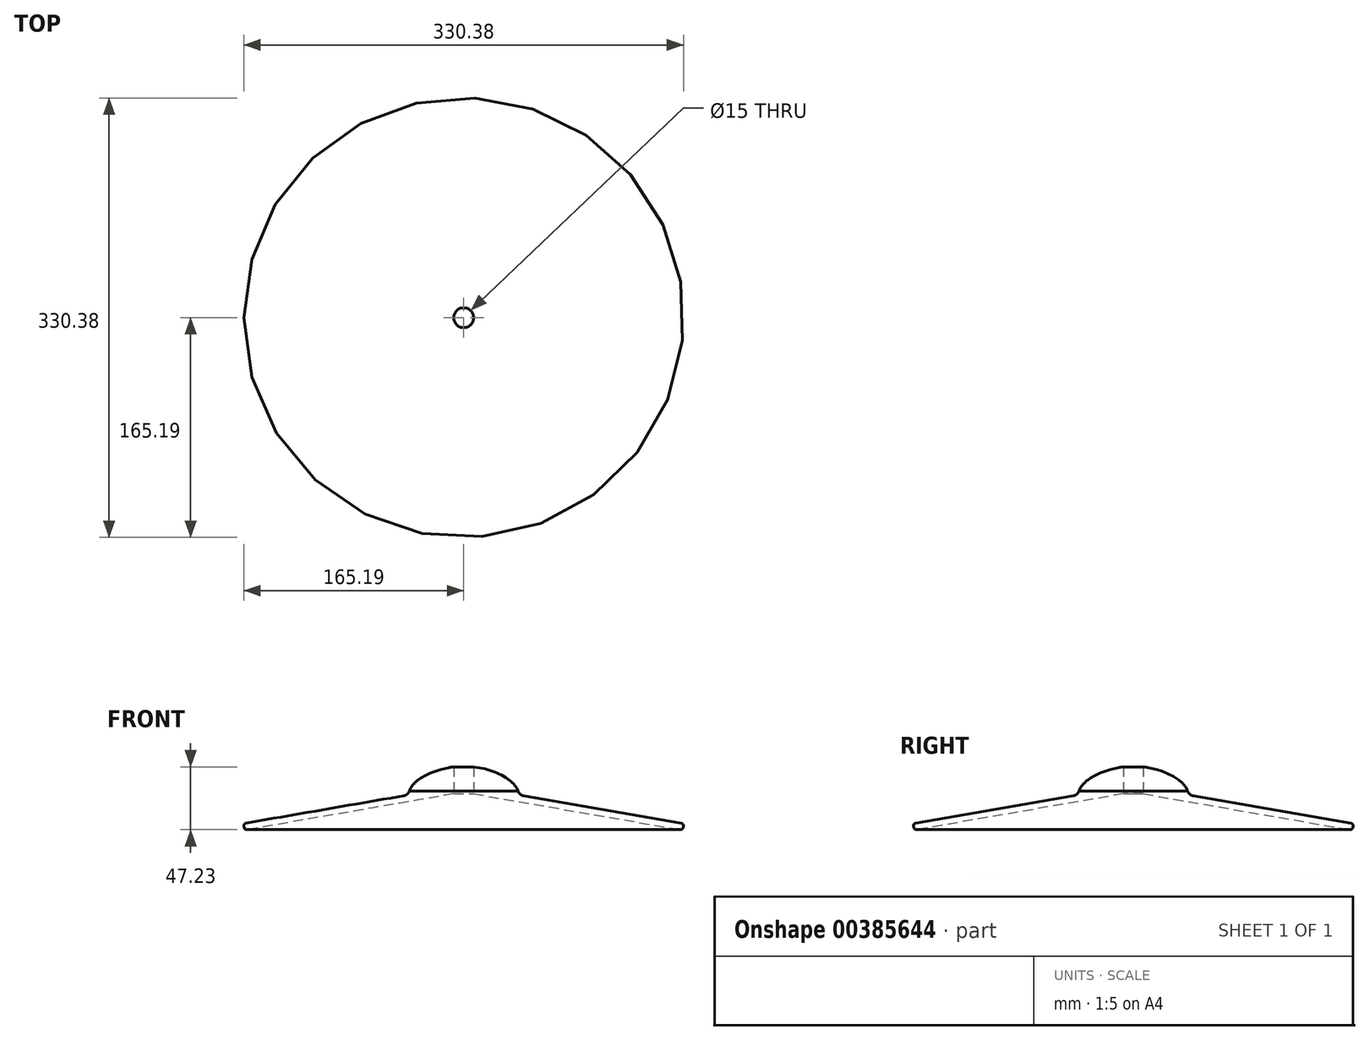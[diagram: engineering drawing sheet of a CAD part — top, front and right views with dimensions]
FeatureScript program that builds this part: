
annotation { "Feature Type Name" : "Feature", "Feature Type Description" : "" }
export const myFeature = defineFeature(function(context is Context, id is Id, definition is map)
    precondition{}
    {
        {
            var Q0;
            Q0=qCreatedBy(makeId("Front.planeOp"),FACE);
            var sketch = newSketch(context, id + "F0", { "sketchPlane" : qUnion([Q0])});
            skLineSegment(sketch, "E0", {"start": v(41.37, 0) * mm, "end": v(165.5, -21.54) * mm});
            skLineSegment(sketch, "E1", {"start": v(165.5, -21.54) * mm, "end": v(164.65, -26.46) * mm});
            skLineSegment(sketch, "E2", {"start": v(164.65, -26.46) * mm, "end": v(0, 2.1) * mm});
            skLineSegment(sketch, "E3", {"start": v(0, 21.54) * mm, "end": v(0, -26.46) * mm, "construction": true});
            skLineSegment(sketch, "E4.bottom", {"start": v(-165.5, 21.54) * mm, "end": v(165.5, 21.54) * mm, "construction": true});
            skLineSegment(sketch, "E4.top", {"start": v(-165.5, -26.46) * mm, "end": v(165.5, -26.46) * mm, "construction": true});
            skLineSegment(sketch, "E4.left", {"start": v(-165.5, 21.54) * mm, "end": v(-165.5, -26.46) * mm, "construction": true});
            skLineSegment(sketch, "E4.right", {"start": v(165.5, 21.54) * mm, "end": v(165.5, -26.46) * mm, "construction": true});
            skLineSegment(sketch, "E5", {"start": v(-41.38, 0) * mm, "end": v(41.38, 0) * mm, "construction": true});
            skLineSegment(sketch, "E6", {"start": v(-41.38, 0) * mm, "end": v(-41.38, 10.77) * mm, "construction": true});
            skLineSegment(sketch, "E7", {"start": v(41.38, 0) * mm, "end": v(41.38, 10.77) * mm, "construction": true});
            skLineSegment(sketch, "E8", {"start": v(-41.38, 10.77) * mm, "end": v(41.38, 10.77) * mm, "construction": true});
            skLineSegment(sketch, "E9", {"start": v(-165.5, -21.54) * mm, "end": v(165.5, -21.54) * mm, "construction": true});
            skLineSegment(sketch, "E10", {"start": v(0, 2.1) * mm, "end": v(0, 21.54) * mm});
            skLineSegment(sketch, "E11", {"start": v(20.69, 21.54) * mm, "end": v(20.69, 0) * mm, "construction": true});
            skFitSpline(sketch, "E12", {"points": [v(0, 21.54) * mm, v(41.38, 0) * mm], "startDerivative": vector(62.06, 0) * mm, "endDerivative": vector(0, -32.3) * mm});
            skSolve(sketch);
        }
        {
            var Q0;
            Q0 = qSketchRegion(id + "F0", true);
            var Q1;
            Q1=sQuery(id+"F0.wireOp",EDGE,"E3");
            revolve(context, id + "F1", {"entities" : qUnion([Q0]), "axis" : qUnion([Q1]), "revolveType" : RevolveType.FULL});
        }
        {
            var Q0;
            Q0=qCreatedBy(makeId("Top.planeOp"),FACE);
            var sketch = newSketch(context, id + "F2", { "sketchPlane" : qUnion([Q0])});
            skCircle(sketch, "E13", {"center": v(0, 0) * mm, "radius": 7.5 * mm});
            skSolve(sketch);
        }
        {
            var Q0;
            Q0 = qSketchRegion(id + "F2", true);
            extrude(context, id + "F3", {"entities" : qUnion([Q0]), "operationType" : NewBodyOperationType.REMOVE, "endBound" : BoundingType.THROUGH_ALL, "depth" : 25 * mm, "hasSecondDirection" : true, "secondDirectionBound" : SecondDirectionBoundingType.THROUGH_ALL, "secondDirectionOppositeDirection" : true, "secondDirectionDepth" : 25 * mm});
        }
        {
            var Q0;
            Q0=makeQuery(id+"F1.opRevolve","SWEPT_EDGE",EDGE,{"disambiguationData":[OSD([sQuery(id+"F0.wireOp",EDGE,"E1"),sQuery(id+"F0.wireOp",EDGE,"E2")])]});
            var Q1;
            Q1=makeQuery(id+"F1.opRevolve","SWEPT_EDGE",EDGE,{"disambiguationData":[OSD([sQuery(id+"F0.wireOp",EDGE,"E0"),sQuery(id+"F0.wireOp",EDGE,"E1")])]});
            fillet(context, id + "F4", {"entities" : qUnion([Q0, Q1]), "radius" : 2 * mm, "tangentPropagation" : true, "allowEdgeOverflow" : false});
        }
        {
            var Q0;
            Q0=makeQuery(id+"F1.opRevolve","SWEPT_EDGE",EDGE,{"disambiguationData":[OSD([sQuery(id+"F0.wireOp",EDGE,"E0"),sQuery(id+"F0.wireOp",EDGE,"E12")])]});
            fillet(context, id + "F5", {"entities" : qUnion([Q0]), "radius" : 5 * mm, "tangentPropagation" : true, "allowEdgeOverflow" : false});
        }
    });
